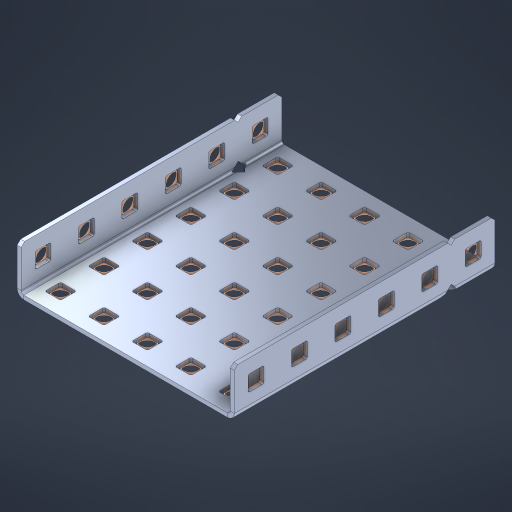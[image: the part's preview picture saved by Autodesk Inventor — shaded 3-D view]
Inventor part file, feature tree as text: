
AUTODESK INVENTOR PART (.ipt)
format: ipt  version: 2023 (Build 270158000, 158)  size: 793,088 bytes
history: native  units: in
note: dims shown in document units (in); Inventor stores cm internally (conversion verified against a paired STEP export)
features: other x47, extrude x41, sheet_metal_op x10, sketch x8, mirror x1, pattern_linear x1, chamfer x1
ambient origin geometry x8: Origin, YZ Plane, XZ Plane, XY Plane, X Axis, Y Axis, Z Axis, Center Point
bodies: Solid1 (feature_tree), Body (feature_tree)
feature tree (109):
  other  "Flange Pattern Plane"
  sheet_metal_op  "Flange Pattern"
  sheet_metal_op  "Body Pattern"
  other  "Arc Length"
  mirror  "Notch Mirror"
  pattern_linear  "Notch Pattern"  Spacing1=0.1875in  [1 undecoded]
  chamfer  "End Chamfer"
  extrude  "Half Cut"  Depth=0.0469in
  sketch  "Sketch1"  dims[d0=2.5in]
  other  "Plate1"
  sketch  "Sketch2"  dims[d1=3.0in]
  other  "Plate2"
  sheet_metal_op  "Bend1"
  sheet_metal_op  "Corner1"
  sketch  "Sketch3"  dims[d2=0.0469in]
  other  "Flange Pattern Sketch"
  sketch  "Sketch7"  dims[d3=0.0469in]
  other  "Srf1"
  other  "Srf2"
  sketch  "Sketch8"  dims[d4=0.0234in]
  sketch  "Sketch9"  dims[d5=0.0938in]
  other  "Srf91"
  sheet_metal_op  "Body Pattern Sketch"
  other  "Srf92"
  sketch  "Sketch13"  dims[d6=0.0469in]
  sketch  "Sketch14"  dims[d7=0.5in d8=90.0deg d9=0.0312in d10=0.1875in d11=0.0469in d12=0.0469in d16=0.182in d17=0.02in d18=0.0469in d19=0.0in d20=0.25in d21=0.25in d46=0.172in d47=1.0in d48=0.0in d49=0.182in d50=0.02in d51=0.25in d52=0.25in d53=0.0469in d54=0.0in d55=0.172in d56=1.0in d57=0.0in d60=2.3622in d62=0.5in d63=1.9685in d65=0.5in d85=0.1227in d86=0.1659in d88=0.04in d89=0.0469in d90=0.0in d91=0.04in d92=0.0491in d95=2.5in d96=0.04in d97=0.25in d98=45.0deg d101=0.0in d102=2.497in d131=2.5in d132=2.3622in d134=0.5in d139=0.5in]
  other  "Srf856"
  other  "Srf1310"
  other  "Srf1311"
  other  "Srf1312"
  other  "Srf1376"
  other  "Srf1377"
  other  "Srf1728"
  other  "Srf1755"
  other  "Srf1878"
  other  "Srf1879"
  other  "Srf1880"
  other  "Srf1881"
  other  "Srf1882"
  other  "Srf1883"
  other  "Srf1942"
  other  "Srf1943"
  other  "Srf1944"
  other  "Srf1945"
  other  "Srf1946"
  other  "Srf1947"
  other  "Srf1948"
  other  "Srf1949"
  other  "Srf1950"
  other  "Srf1951"
  other  "Srf1952"
  other  "Srf1953"
  other  "Srf1954"
  other  "Srf1955"
  other  "Srf1956"
  other  "Srf1957"
  other  "Srf1958"
  other  "Srf1959"
  other  "Srf1960"
  other  "Srf1961"
  other  "Srf1962"
  other  "Srf1963"
  other  "Srf1964"
  other  "Srf1965"
  sheet_metal_op  "Flange Stamp"
  sheet_metal_op  "Flange Circle"
  sheet_metal_op  "Body Stamp"
  sheet_metal_op  "Body Circle"
  sheet_metal_op  "Notch"
  extrude  "ExtrusionSrf2"  Depth=0.0469in
  extrude  "ExtrusionSrf92"  Depth=2.5in
  extrude  "ExtrusionSrf856"  Depth=0.02in
  extrude  "ExtrusionSrf1310"  Depth=0.0469in
  extrude  "ExtrusionSrf1311"  TaperAngle=0.0deg  [1 undecoded]
  extrude  "ExtrusionSrf1312"  Depth=0.25in
  extrude  "ExtrusionSrf1376"  Depth=0.25in
  extrude  "ExtrusionSrf1377"  Depth=2.5in
  extrude  "ExtrusionSrf1728"  Depth=2.5in TaperAngle=0.0deg
  extrude  "ExtrusionSrf1755"  Depth=2.5in
  extrude  "ExtrusionSrf1878"  Depth=0.02in
  extrude  "ExtrusionSrf1879"  Depth=0.25in
  extrude  "ExtrusionSrf1880"  Depth=0.25in
  extrude  "ExtrusionSrf1881"  Depth=0.0469in
  extrude  "ExtrusionSrf1882"  TaperAngle=0.0deg  [1 undecoded]
  extrude  "ExtrusionSrf1883"  Depth=2.5in
  extrude  "ExtrusionSrf1942"  Depth=2.5in TaperAngle=0.0deg
  extrude  "ExtrusionSrf1943"  Depth=2.5in
  extrude  "ExtrusionSrf1944"  Depth=2.5in
  extrude  "ExtrusionSrf1945"  Depth=2.5in
  extrude  "ExtrusionSrf1946"  Depth=2.5in
  extrude  "ExtrusionSrf1947"  Depth=2.5in
  extrude  "ExtrusionSrf1948"  Depth=0.0469in
  extrude  "ExtrusionSrf1949"  TaperAngle=0.0deg  [1 undecoded]
  extrude  "ExtrusionSrf1950"  Depth=2.5in
  extrude  "ExtrusionSrf1951"  Depth=2.5in
  extrude  "ExtrusionSrf1952"  Depth=2.5in
  extrude  "ExtrusionSrf1953"  Depth=0.25in TaperAngle=45.0deg
  extrude  "ExtrusionSrf1954"  TaperAngle=0.0deg  [1 undecoded]
  extrude  "ExtrusionSrf1955"  Depth=2.5in
  extrude  "ExtrusionSrf1956"  Depth=2.5in
  extrude  "ExtrusionSrf1957"  Depth=2.5in
  extrude  "ExtrusionSrf1958"  Depth=2.5in
  extrude  "ExtrusionSrf1959"  Depth=2.5in
  extrude  "ExtrusionSrf1960"  [1 undecoded]
  extrude  "ExtrusionSrf1961"  [1 undecoded]
  extrude  "ExtrusionSrf1962"  [1 undecoded]
  extrude  "ExtrusionSrf1963"  [1 undecoded]
  extrude  "ExtrusionSrf1964"  [1 undecoded]
  extrude  "ExtrusionSrf1965"  [1 undecoded]
note: 11 required parameter values undecoded (feature->parameter linkage not recoverable at this tier; creation-order binding heuristic only, values carry confidence <= 0.55)
